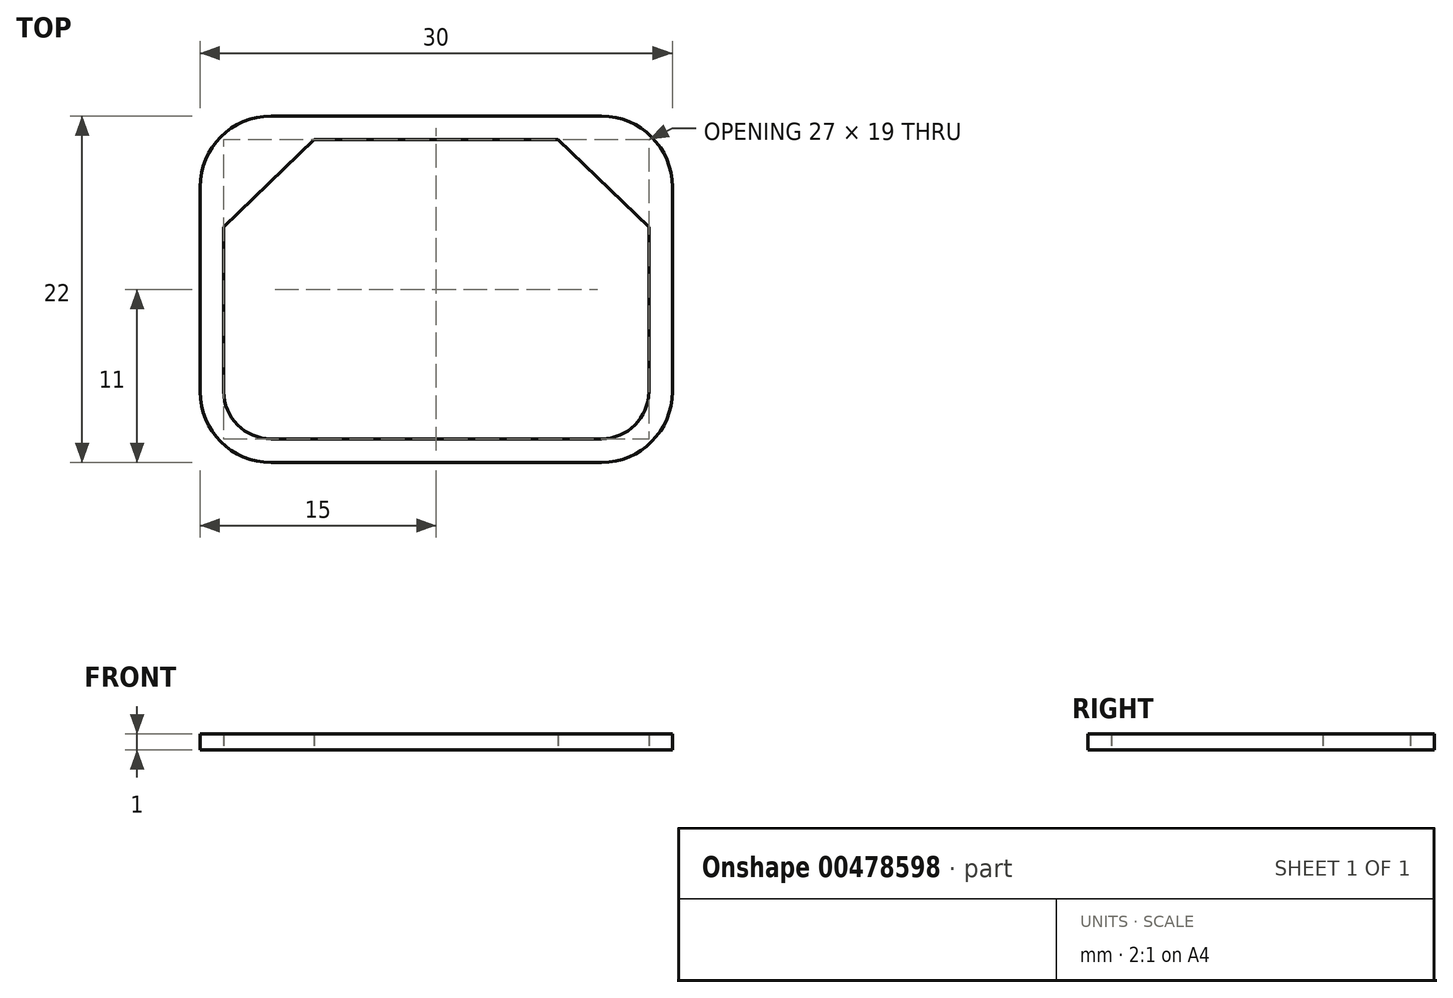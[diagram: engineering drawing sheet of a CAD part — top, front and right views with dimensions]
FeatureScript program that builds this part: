
annotation { "Feature Type Name" : "Feature", "Feature Type Description" : "" }
export const myFeature = defineFeature(function(context is Context, id is Id, definition is map)
    precondition{}
    {
        {
            var Q0;
            Q0=qCreatedBy(makeId("Top.planeOp"),FACE);
            var sketch = newSketch(context, id + "F0", { "sketchPlane" : qUnion([Q0])});
            skLineSegment(sketch, "E0.bottom", {"start": v(15, 11) * mm, "end": v(-15, 11) * mm});
            skLineSegment(sketch, "E0.top", {"start": v(15, -11) * mm, "end": v(-15, -11) * mm});
            skLineSegment(sketch, "E0.left", {"start": v(15, 11) * mm, "end": v(15, -11) * mm});
            skLineSegment(sketch, "E0.right", {"start": v(-15, 11) * mm, "end": v(-15, -11) * mm});
            skPoint(sketch, "E0.middle", {"position": v(0, 0) * mm});
            skLineSegment(sketch, "E1.bottom", {"start": v(13.5, 9.5) * mm, "end": v(-13.5, 9.5) * mm});
            skLineSegment(sketch, "E1.top", {"start": v(13.5, -9.5) * mm, "end": v(-13.5, -9.5) * mm});
            skLineSegment(sketch, "E1.left", {"start": v(13.5, 9.5) * mm, "end": v(13.5, -9.5) * mm});
            skLineSegment(sketch, "E1.right", {"start": v(-13.5, 9.5) * mm, "end": v(-13.5, -9.5) * mm});
            skLineSegment(sketch, "E2", {"start": v(7.75, 9.5) * mm, "end": v(13.5, 3.94) * mm});
            skLineSegment(sketch, "E3", {"start": v(-7.75, 9.5) * mm, "end": v(-13.5, 3.94) * mm});
            skSolve(sketch);
        }
        {
            var Q0;
            Q0 = qSketchRegion(id + "F0", true);
            var Q1;
            {var subQ3=sQuery(id+"F0.wireOp",EDGE,"E3");Q1=makeQuery(id+"F0.imprint","IMPRINT",FACE,{"disambiguationData":[TD([[makeQuery(id+"F0.imprint","IMPRINT",EDGE,{"derivedFrom":subQ3}),-1.0]])]});}
            var Q2;
            {var subQ3=sQuery(id+"F0.wireOp",EDGE,"E2");Q2=makeQuery(id+"F0.imprint","IMPRINT",FACE,{"disambiguationData":[TD([[makeQuery(id+"F0.imprint","IMPRINT",EDGE,{"derivedFrom":subQ3}),1.0]])]});}
            extrude(context, id + "F1", {"entities" : qUnion([Q0, Q1, Q2]), "depth" : 1 * mm});
        }
        {
            var Q0;
            Q0=makeQuery(id+"F1.opExtrude","SWEPT_EDGE",EDGE,{"disambiguationData":[OSD([sQuery(id+"F0.wireOp",EDGE,"E1.top"),sQuery(id+"F0.wireOp",EDGE,"E1.left")])]});
            var Q1;
            Q1=makeQuery(id+"F1.opExtrude","SWEPT_EDGE",EDGE,{"disambiguationData":[OSD([sQuery(id+"F0.wireOp",EDGE,"E1.top"),sQuery(id+"F0.wireOp",EDGE,"E1.right")])]});
            fillet(context, id + "F2", {"entities" : qUnion([Q0, Q1]), "radius" : 3 * mm, "tangentPropagation" : true, "allowEdgeOverflow" : false});
        }
        {
            var Q0;
            Q0=makeQuery(id+"F1.opExtrude","SWEPT_EDGE",EDGE,{"disambiguationData":[OSD([sQuery(id+"F0.wireOp",EDGE,"E0.top"),sQuery(id+"F0.wireOp",EDGE,"E0.left")])]});
            var Q1;
            Q1=makeQuery(id+"F1.opExtrude","SWEPT_EDGE",EDGE,{"disambiguationData":[OSD([sQuery(id+"F0.wireOp",EDGE,"E0.bottom"),sQuery(id+"F0.wireOp",EDGE,"E0.left")])]});
            var Q2;
            Q2=makeQuery(id+"F1.opExtrude","SWEPT_EDGE",EDGE,{"disambiguationData":[OSD([sQuery(id+"F0.wireOp",EDGE,"E0.top"),sQuery(id+"F0.wireOp",EDGE,"E0.right")])]});
            var Q3;
            Q3=makeQuery(id+"F1.opExtrude","SWEPT_EDGE",EDGE,{"disambiguationData":[OSD([sQuery(id+"F0.wireOp",EDGE,"E0.bottom"),sQuery(id+"F0.wireOp",EDGE,"E0.right")])]});
            fillet(context, id + "F3", {"entities" : qUnion([Q0, Q1, Q2, Q3]), "radius" : 4.5 * mm, "tangentPropagation" : true, "allowEdgeOverflow" : false});
        }
    });
